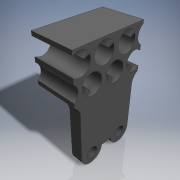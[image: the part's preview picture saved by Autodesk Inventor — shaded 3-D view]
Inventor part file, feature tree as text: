
AUTODESK INVENTOR PART (.ipt)
format: ipt  version: 2016 (Build 200138000, 138)  size: 310,784 bytes
history: native  units: in
note: dims shown in document units (in); Inventor stores cm internally (conversion verified against a paired STEP export)
features: reference x25, extrude x4, sketch x4, fillet x1, projected_geometry x1
ambient origin geometry x8: Origin, YZ Plane, XZ Plane, XY Plane, X Axis, Y Axis, Z Axis, Center Point
bodies: Body1 (feature_tree)
feature tree (35):
  extrude  "Extrusion2"  Depth=0.1299in
  sketch  "Sketch2"  dims[d2=0.1299in d3=0.1299in]
  extrude  "Extrusion4"  Depth=0.1299in
  extrude  "Extrusion5"  Depth=0.1299in
  fillet  "Fillet1"  Radius=0.1592in
  extrude  "Extrusion6"  Depth=0.0787in
  sketch  "Sketch1"  dims[d0=0.1299in d1=0.1299in]
  reference  "Reference1"
  reference  "Reference2"
  reference  "Reference3"
  reference  "Reference4"
  reference  "Reference5"
  reference  "Reference6"
  reference  "Reference7"
  reference  "Reference8"
  reference  "Reference9"
  reference  "Reference10"
  reference  "Reference11"
  reference  "Reference12"
  reference  "Reference13"
  reference  "Reference14"
  reference  "Reference15"
  reference  "Reference16"
  reference  "Reference17"
  reference  "Reference18"
  reference  "Reference19"
  reference  "Reference20"
  reference  "Reference21"
  sketch  "Sketch3"  dims[d4=0.1299in d5=0.1299in d6=0.1592in]
  reference  "Reference22"
  reference  "Reference23"
  reference  "Reference24"
  reference  "Reference25"
  sketch  "Sketch4"  dims[d7=0.154in d8=0.1592in d9=0.154in d10=0.1299in d11=0.154in d14=0.1299in d15=0.154in d16=0.1969in d17=0.0in d18=0.2886in d19=0.2886in d20=0.2886in d21=0.2886in d23=0.2886in d24=0.2886in d25=15.0deg d26=15.0deg d27=15.0deg d28=15.0deg d29=15.0deg d30=0.0591in d31=0.0591in d32=0.0591in d33=0.0591in d34=0.0591in d35=0.0591in d38=0.0787in d39=0.0in d40=0.0591in d41=0.0in d42=0.0787in d43=0.0787in d44=0.0in]
  projected_geometry  "Projected Loop1"
